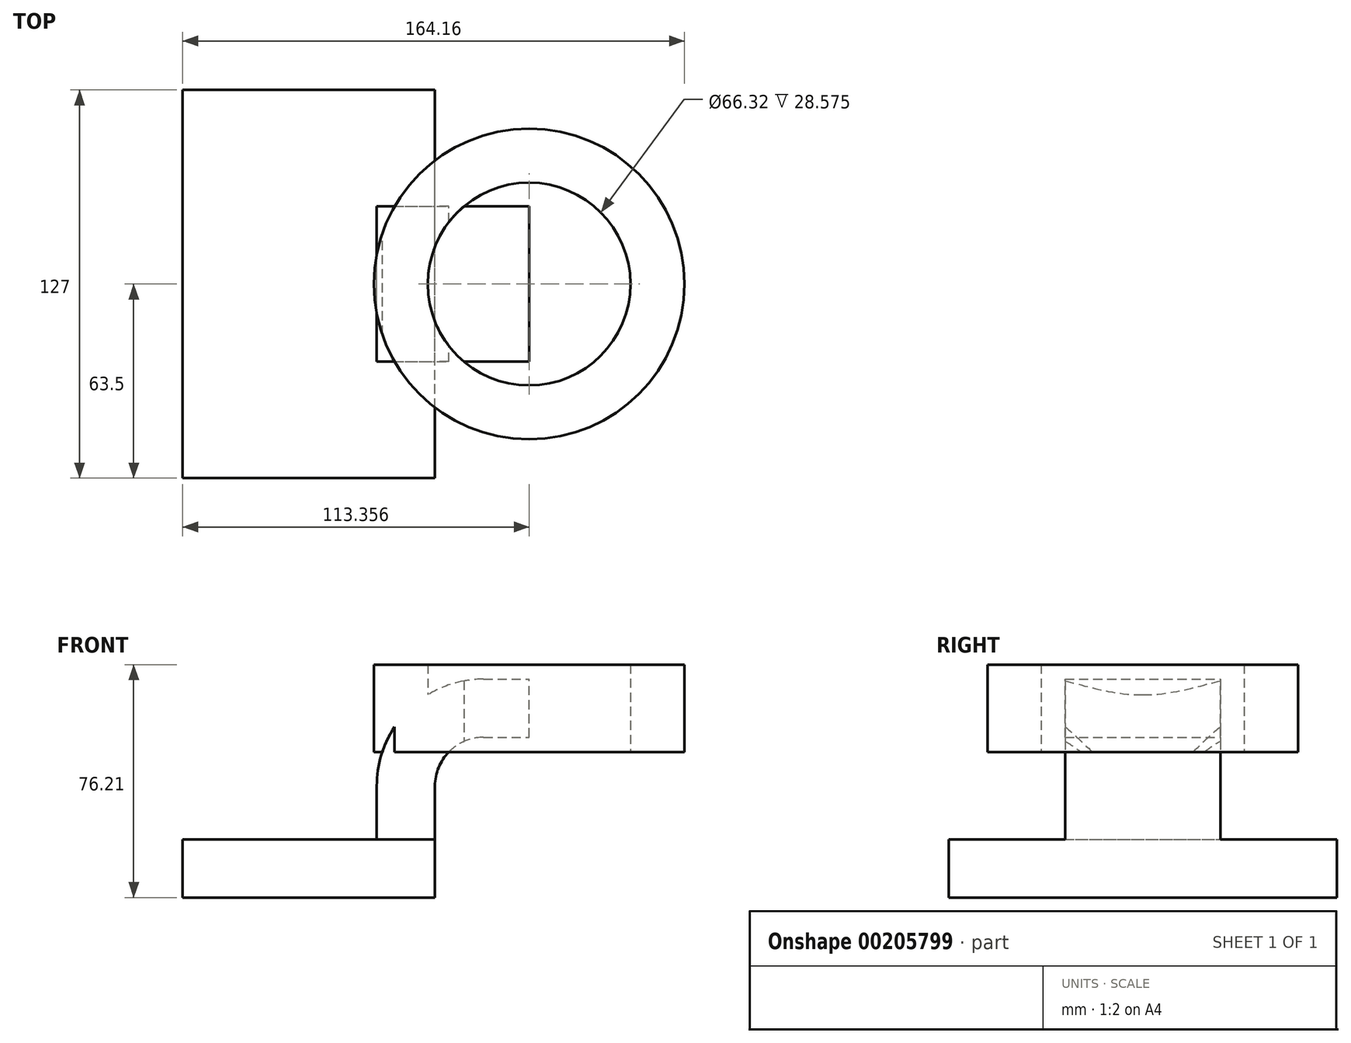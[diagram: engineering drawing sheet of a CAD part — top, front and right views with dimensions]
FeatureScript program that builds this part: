
annotation { "Feature Type Name" : "Feature", "Feature Type Description" : "" }
export const myFeature = defineFeature(function(context is Context, id is Id, definition is map)
    precondition{}
    {
        {
            var Q0;
            Q0=qCreatedBy(makeId("Front.planeOp"),FACE);
            var sketch = newSketch(context, id + "F0", { "sketchPlane" : qUnion([Q0])});
            skLineSegment(sketch, "E0.bottom", {"start": v(-41.28, -9.53) * mm, "end": v(41.28, -9.53) * mm});
            skLineSegment(sketch, "E0.top", {"start": v(-41.28, 9.52) * mm, "end": v(41.28, 9.52) * mm});
            skLineSegment(sketch, "E0.left", {"start": v(-41.27, -9.53) * mm, "end": v(-41.28, 9.52) * mm});
            skLineSegment(sketch, "E0.right", {"start": v(41.28, -9.53) * mm, "end": v(41.28, 9.52) * mm});
            skPoint(sketch, "E0.middle", {"position": v(0, 0) * mm});
            skLineSegment(sketch, "E1.bottom", {"start": v(72.08, 38.1) * mm, "end": v(122.88, 38.1) * mm});
            skLineSegment(sketch, "E1.top", {"start": v(72.08, 66.67) * mm, "end": v(122.88, 66.67) * mm});
            skLineSegment(sketch, "E1.left", {"start": v(72.08, 38.1) * mm, "end": v(72.08, 66.67) * mm});
            skLineSegment(sketch, "E1.right", {"start": v(122.88, 38.1) * mm, "end": v(122.88, 66.67) * mm});
            skPoint(sketch, "E1.middle", {"position": v(97.48, 52.39) * mm});
            skLineSegment(sketch, "E2", {"start": v(41.27, 9.52) * mm, "end": v(41.27, 27) * mm});
            skArc(sketch, "E3", {"start": v(41.27, 27) * mm, "mid": v(45.92, 38.23) * mm, "end": v(57.15, 42.88) * mm});
            skLineSegment(sketch, "E4", {"start": v(57.15, 42.88) * mm, "end": v(105.23, 42.88) * mm});
            skLineSegment(sketch, "E5.0", {"start": v(57.15, 61.93) * mm, "end": v(105.23, 61.93) * mm});
            skArc(sketch, "E5.1", {"start": v(22.22, 27) * mm, "mid": v(32.45, 51.7) * mm, "end": v(57.15, 61.93) * mm});
            skLineSegment(sketch, "E5.2", {"start": v(22.22, 9.52) * mm, "end": v(22.22, 27) * mm});
            skLineSegment(sketch, "E6", {"start": v(105.23, 38.1) * mm, "end": v(105.23, 66.67) * mm});
            skFitSpline(sketch, "E7", {"points": [v(-41.28, 9.52) * mm, v(57.15, 61.93) * mm], "startDerivative": vector(9.38, 89.1) * mm, "endDerivative": vector(126.43, -2.45) * mm});
            skSolve(sketch);
        }
        {
            var Q0;
            Q0=makeQuery(id+"F0.imprint","IMPRINT",FACE,{"disambiguationData":[TD([[makeQuery(id+"F0.imprint","IMPRINT",EDGE,{"derivedFrom":sQuery(id+"F0.wireOp",EDGE,"E0.bottom")}),1.0]])]});
            extrude(context, id + "F1", {"entities" : qUnion([Q0]), "endBound" : BoundingType.SYMMETRIC, "depth" : 127 * mm});
        }
        {
            var Q0;
            {var subQ1=sQuery(id+"F0.wireOp",EDGE,"E2");Q0=makeQuery(id+"F0.imprint","IMPRINT",FACE,{"disambiguationData":[TD([[makeQuery(id+"F0.imprint","IMPRINT",EDGE,{"derivedFrom":subQ1}),1.0]])]});}
            extrude(context, id + "F2", {"entities" : qUnion([Q0]), "operationType" : NewBodyOperationType.ADD, "endBound" : BoundingType.SYMMETRIC, "depth" : 50.8 * mm});
        }
        {
            var Q0;
            Q0=makeQuery(id+"F0.imprint","IMPRINT",FACE,{"disambiguationData":[TD([[makeQuery(id+"F0.imprint","IMPRINT",EDGE,{"derivedFrom":sQuery(id+"F0.wireOp",EDGE,"E5.1")}),1.0]])]});
            extrude(context, id + "F3", {"entities" : qUnion([Q0]), "operationType" : NewBodyOperationType.ADD, "endBound" : BoundingType.SYMMETRIC, "depth" : 15.88 * mm});
        }
        {
            var Q0;
            {var subQ0=sQuery(id+"F0.wireOp",EDGE,"E1.right");Q0=makeQuery(id+"F0.imprint","IMPRINT",FACE,{"disambiguationData":[TD([[makeQuery(id+"F0.imprint","IMPRINT",EDGE,{"derivedFrom":subQ0}),1.0]])]});}
            var Q1;
            Q1=sQuery(id+"F0.wireOp",EDGE,"E1.left");
            revolve(context, id + "F4", {"operationType" : NewBodyOperationType.ADD, "entities" : qUnion([Q0]), "axis" : qUnion([Q1]), "revolveType" : RevolveType.FULL});
        }
    });
